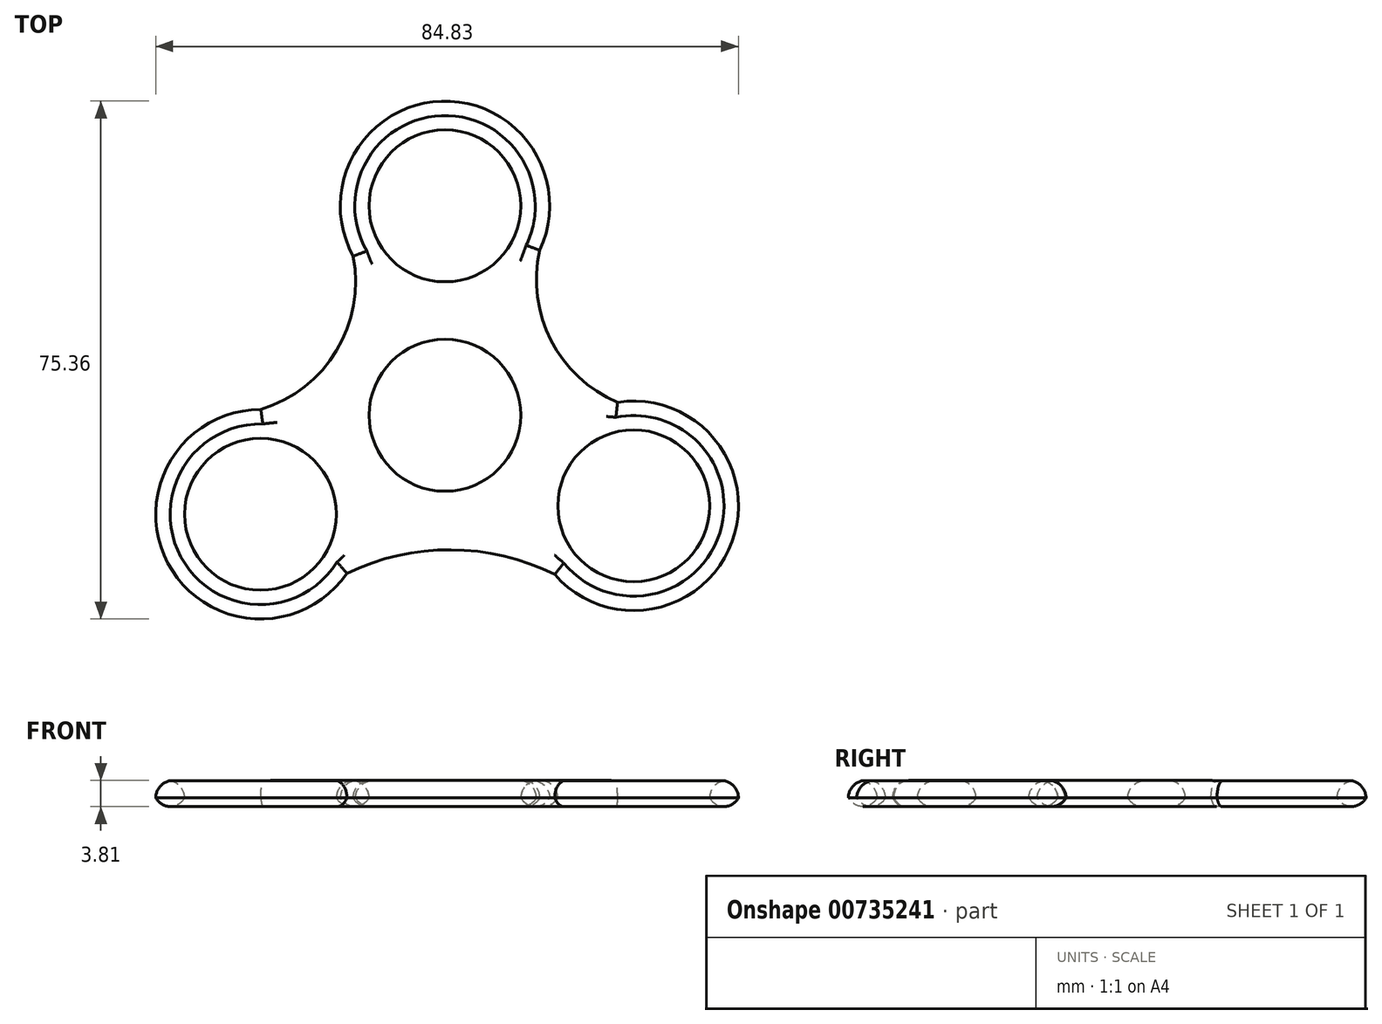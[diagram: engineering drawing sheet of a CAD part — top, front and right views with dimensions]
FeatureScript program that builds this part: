
annotation { "Feature Type Name" : "Feature", "Feature Type Description" : "" }
export const myFeature = defineFeature(function(context is Context, id is Id, definition is map)
    precondition{}
    {
        {
            var Q0;
            Q0=qCreatedBy(makeId("Top.planeOp"),FACE);
            var sketch = newSketch(context, id + "F0", { "sketchPlane" : qUnion([Q0])});
            skCircle(sketch, "E0", {"center": v(0, 0) * mm, "radius": 11.05 * mm});
            skCircle(sketch, "E1", {"center": v(0, 0) * mm, "radius": 13.97 * mm});
            skLineSegment(sketch, "E2", {"start": v(0, 0) * mm, "end": v(0, 30.48) * mm});
            skCircle(sketch, "E3", {"center": v(0, 30.48) * mm, "radius": 11.05 * mm});
            skCircle(sketch, "E4", {"center": v(0, 30.48) * mm, "radius": 15.24 * mm});
            skLineSegment(sketch, "E5", {"start": v(0, 0) * mm, "end": v(-26.86, -14.4) * mm});
            skCircle(sketch, "E6", {"center": v(-26.86, -14.4) * mm, "radius": 11.05 * mm});
            skCircle(sketch, "E7", {"center": v(-26.86, -14.4) * mm, "radius": 15.24 * mm});
            skLineSegment(sketch, "E8", {"start": v(0, 0) * mm, "end": v(27.49, -13.17) * mm});
            skCircle(sketch, "E9", {"center": v(27.49, -13.17) * mm, "radius": 11.05 * mm});
            skCircle(sketch, "E10", {"center": v(27.49, -13.17) * mm, "radius": 15.24 * mm});
            skArc(sketch, "E11", {"start": v(13.8, 24.03) * mm, "mid": v(15.45, 10.9) * mm, "end": v(25.13, 1.88) * mm});
            skArc(sketch, "E12", {"start": v(15.98, -23.17) * mm, "mid": v(0.87, -19.56) * mm, "end": v(-14.28, -23) * mm});
            skArc(sketch, "E13", {"start": v(-26.81, 0.84) * mm, "mid": v(-15.8, 9.42) * mm, "end": v(-13.37, 23.17) * mm});
            skSolve(sketch);
        }
        {
            var Q0;
            Q0=makeQuery(id+"F0.imprint","IMPRINT",FACE,{"disambiguationData":[TD([[makeQuery(id+"F0.imprint","IMPRINT",EDGE,{"derivedFrom":sQuery(id+"F0.wireOp",EDGE,"E3")}),-1.0]])]});
            var Q1;
            {var subQ5=sQuery(id+"F0.wireOp",EDGE,"E13");Q1=makeQuery(id+"F0.imprint","IMPRINT",FACE,{"disambiguationData":[TD([[makeQuery(id+"F0.imprint","IMPRINT",EDGE,{"derivedFrom":subQ5}),-1.0]])]});}
            var Q2;
            {var subQ5=sQuery(id+"F0.wireOp",EDGE,"E11");Q2=makeQuery(id+"F0.imprint","IMPRINT",FACE,{"disambiguationData":[TD([[makeQuery(id+"F0.imprint","IMPRINT",EDGE,{"derivedFrom":subQ5}),-1.0]])]});}
            var Q3;
            {var subQ0=sQuery(id+"F0.wireOp",EDGE,"E2");var subQ1=sQuery(id+"F0.wireOp",EDGE,"E0");var subQ2=makeQuery(id+"F0.imprint","INTERSECT",VERTEX,{"derivedFrom":[subQ1,subQ0]});Q3=makeQuery(id+"F0.imprint","IMPRINT",FACE,{"disambiguationData":[TD([[makeQuery(id+"F0.imprint","IMPRINT",EDGE,{"disambiguationData":[TD([[subQ2,1.0]])],"derivedFrom":subQ1}),-1.0]])]});}
            var Q4;
            {var subQ0=sQuery(id+"F0.wireOp",EDGE,"E5");var subQ1=sQuery(id+"F0.wireOp",EDGE,"E0");var subQ2=makeQuery(id+"F0.imprint","INTERSECT",VERTEX,{"derivedFrom":[subQ1,subQ0]});Q4=makeQuery(id+"F0.imprint","IMPRINT",FACE,{"disambiguationData":[TD([[makeQuery(id+"F0.imprint","IMPRINT",EDGE,{"disambiguationData":[TD([[subQ2,-1.0]])],"derivedFrom":subQ1}),-1.0]])]});}
            var Q5;
            {var subQ0=sQuery(id+"F0.wireOp",EDGE,"E5");var subQ1=sQuery(id+"F0.wireOp",EDGE,"E0");var subQ2=makeQuery(id+"F0.imprint","INTERSECT",VERTEX,{"derivedFrom":[subQ1,subQ0]});Q5=makeQuery(id+"F0.imprint","IMPRINT",FACE,{"disambiguationData":[TD([[makeQuery(id+"F0.imprint","IMPRINT",EDGE,{"disambiguationData":[TD([[subQ2,1.0]])],"derivedFrom":subQ1}),-1.0]])]});}
            var Q6;
            {var subQ9=sQuery(id+"F0.wireOp",EDGE,"E12");Q6=makeQuery(id+"F0.imprint","IMPRINT",FACE,{"disambiguationData":[TD([[makeQuery(id+"F0.imprint","IMPRINT",EDGE,{"derivedFrom":subQ9}),-1.0]])]});}
            var Q7;
            Q7=makeQuery(id+"F0.imprint","IMPRINT",FACE,{"disambiguationData":[TD([[makeQuery(id+"F0.imprint","IMPRINT",EDGE,{"derivedFrom":sQuery(id+"F0.wireOp",EDGE,"E6")}),-1.0]])]});
            var Q8;
            Q8=makeQuery(id+"F0.imprint","IMPRINT",FACE,{"disambiguationData":[TD([[makeQuery(id+"F0.imprint","IMPRINT",EDGE,{"derivedFrom":sQuery(id+"F0.wireOp",EDGE,"E9")}),-1.0]])]});
            extrude(context, id + "F1", {"entities" : qUnion([Q0, Q1, Q2, Q3, Q4, Q5, Q6, Q7, Q8]), "depth" : 3.8 * mm, "offsetDistance" : 25.4 * mm});
        }
        {
            var Q0;
            Q0=makeQuery(id+"F1.opExtrude","CAP_EDGE",EDGE,{"disambiguationData":[OSD([sQuery(id+"F0.wireOp",EDGE,"E12")])],"isStart":false});
            var Q1;
            Q1=makeQuery(id+"F1.opExtrude","CAP_EDGE",EDGE,{"disambiguationData":[OSD([sQuery(id+"F0.wireOp",EDGE,"E0")])],"isStart":false});
            var Q2;
            Q2=makeQuery(id+"F1.opExtrude","CAP_EDGE",EDGE,{"disambiguationData":[OSD([sQuery(id+"F0.wireOp",EDGE,"E9")])],"isStart":false});
            var Q3;
            Q3=makeQuery(id+"F1.opExtrude","CAP_EDGE",EDGE,{"disambiguationData":[OSD([sQuery(id+"F0.wireOp",EDGE,"E3")])],"isStart":false});
            var Q4;
            Q4=makeQuery(id+"F1.opExtrude","CAP_FACE",FACE,{"disambiguationData":[OSD([sQuery(id+"F0.wireOp",EDGE,"E0"),sQuery(id+"F0.wireOp",EDGE,"E3"),sQuery(id+"F0.wireOp",EDGE,"E4"),sQuery(id+"F0.wireOp",EDGE,"E6"),sQuery(id+"F0.wireOp",EDGE,"E7"),sQuery(id+"F0.wireOp",EDGE,"E9"),sQuery(id+"F0.wireOp",EDGE,"E10"),sQuery(id+"F0.wireOp",EDGE,"E11"),sQuery(id+"F0.wireOp",EDGE,"E12"),sQuery(id+"F0.wireOp",EDGE,"E13")])],"isStart":false});
            fillet(context, id + "F2", {"entities" : qUnion([Q0, Q1, Q2, Q3, Q4]), "radius" : 2.54 * mm, "tangentPropagation" : true, "allowEdgeOverflow" : false});
        }
        {
            var Q0;
            Q0=makeQuery(id+"F1.opExtrude","CAP_EDGE",EDGE,{"disambiguationData":[OSD([sQuery(id+"F0.wireOp",EDGE,"E9")])],"isStart":true});
            var Q1;
            Q1=makeQuery(id+"F1.opExtrude","CAP_EDGE",EDGE,{"disambiguationData":[OSD([sQuery(id+"F0.wireOp",EDGE,"E6")])],"isStart":true});
            var Q2;
            Q2=makeQuery(id+"F1.opExtrude","CAP_EDGE",EDGE,{"disambiguationData":[OSD([sQuery(id+"F0.wireOp",EDGE,"E13")])],"isStart":true});
            var Q3;
            Q3=makeQuery(id+"F1.opExtrude","CAP_EDGE",EDGE,{"disambiguationData":[OSD([sQuery(id+"F0.wireOp",EDGE,"E3")])],"isStart":true});
            var Q4;
            {var subQ0=sQuery(id+"F0.wireOp",EDGE,"E0");Q4=makeQuery(id+"F2.opFillet","BLEND_EDGE",EDGE,{"blendedFrom":[makeQuery(id+"F1.opExtrude","CAP_EDGE",EDGE,{"disambiguationData":[OSD([subQ0])],"isStart":false}),makeQuery(id+"F1.opExtrude","SWEPT_FACE",FACE,{"disambiguationData":[OSD([subQ0])]})],"blendedInto":[makeQuery(id+"F1.opExtrude","SWEPT_FACE",FACE,{"disambiguationData":[OSD([subQ0])]})]});}
            var Q5;
            Q5=makeQuery(id+"F1.opExtrude","CAP_EDGE",EDGE,{"disambiguationData":[OSD([sQuery(id+"F0.wireOp",EDGE,"E11")])],"isStart":true});
            var Q6;
            Q6=makeQuery(id+"F1.opExtrude","CAP_EDGE",EDGE,{"disambiguationData":[OSD([sQuery(id+"F0.wireOp",EDGE,"E12")])],"isStart":true});
            fillet(context, id + "F3", {"entities" : qUnion([Q0, Q1, Q2, Q3, Q4, Q5, Q6]), "radius" : 2.54 * mm, "tangentPropagation" : true, "allowEdgeOverflow" : false});
        }
        {
            var Q0;
            Q0=makeQuery(id+"F1.opExtrude","CAP_FACE",FACE,{"disambiguationData":[OSD([sQuery(id+"F0.wireOp",EDGE,"E0"),sQuery(id+"F0.wireOp",EDGE,"E3"),sQuery(id+"F0.wireOp",EDGE,"E4"),sQuery(id+"F0.wireOp",EDGE,"E6"),sQuery(id+"F0.wireOp",EDGE,"E7"),sQuery(id+"F0.wireOp",EDGE,"E9"),sQuery(id+"F0.wireOp",EDGE,"E10"),sQuery(id+"F0.wireOp",EDGE,"E11"),sQuery(id+"F0.wireOp",EDGE,"E12"),sQuery(id+"F0.wireOp",EDGE,"E13")])],"isStart":true});
            fillet(context, id + "F4", {"entities" : qUnion([Q0]), "radius" : 2.54 * mm, "tangentPropagation" : true, "allowEdgeOverflow" : false});
        }
    });
